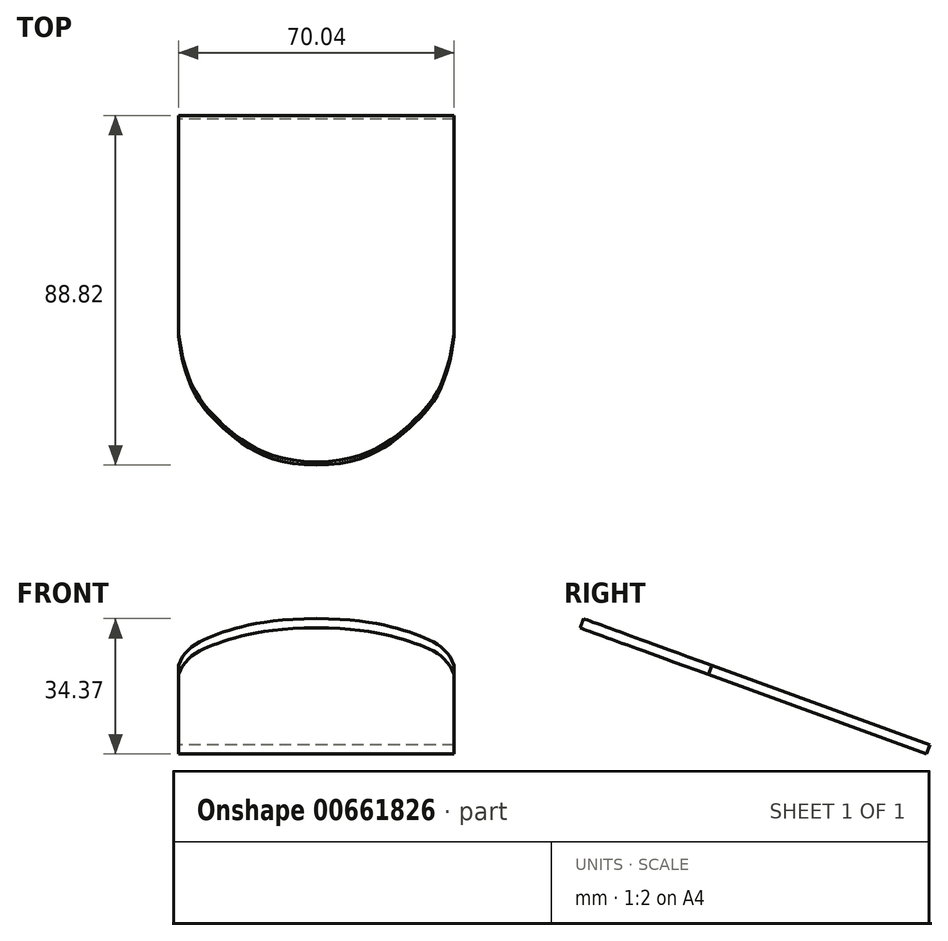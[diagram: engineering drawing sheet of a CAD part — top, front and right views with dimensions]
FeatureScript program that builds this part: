
annotation { "Feature Type Name" : "Feature", "Feature Type Description" : "" }
export const myFeature = defineFeature(function(context is Context, id is Id, definition is map)
    precondition{}
    {
        {
            var Q0;
            Q0=qCreatedBy(makeId("Top.planeOp"),FACE);
            cPlane(context, id + "F0", {"entities" : qUnion([Q0]), "cplaneType" : CPlaneType.OFFSET, "offset" : 20 * mm, "oppositeDirection" : true, "width" : 150 * mm, "height" : 150 * mm});
        }
        {
            var Q0;
            Q0=qCreatedBy(id+"F0.planeOp",FACE);
            cPlane(context, id + "F1", {"entities" : qUnion([Q0]), "cplaneType" : CPlaneType.OFFSET, "offset" : 50 * mm, "oppositeDirection" : true, "width" : 150 * mm, "height" : 150 * mm});
        }
        {
            var Q0;
            Q0=qCreatedBy(makeId("Right.planeOp"),FACE);
            var sketch = newSketch(context, id + "F2", { "sketchPlane" : qUnion([Q0])});
            skLineSegment(sketch, "E0", {"start": v(0, 15.18) * mm, "end": v(0, -94.42) * mm, "construction": true});
            skSolve(sketch);
        }
        {
            var Q0;
            Q0=qCreatedBy(id+"F1.planeOp",FACE);
            var sketch = newSketch(context, id + "F3", { "sketchPlane" : qUnion([Q0])});
            skLineSegment(sketch, "E1", {"start": v(-73.4, 0) * mm, "end": v(89.46, 0) * mm, "construction": true});
            skSolve(sketch);
        }
        {
            var Q0;
            Q0=sQuery(id+"F3.wireOp",EDGE,"E1");
            cPlane(context, id + "F4", {"entities" : qUnion([Q0]), "cplaneType" : CPlaneType.LINE_ANGLE, "offset" : 25 * mm, "angle" : 70 * degree, "width" : 150 * mm, "height" : 150 * mm});
        }
        {
            var Q0;
            Q0=qCreatedBy(id+"F4.planeOp",FACE);
            var sketch = newSketch(context, id + "F5", { "sketchPlane" : qUnion([Q0])});
            skFitSpline(sketch, "E2", {"points": [v(0, -10.76) * mm, v(-24.39, 0) * mm, v(-35.02, 23.96) * mm], "startDerivative": vector(-74.23, -0.1) * mm, "endDerivative": vector(-10.58, 83.32) * mm});
            skFitSpline(sketch, "E3.MirrorCS", {"points": [v(0, -10.76) * mm, v(24.39, 0) * mm, v(35.02, 23.96) * mm], "startDerivative": vector(74.23, -0.1) * mm, "endDerivative": vector(10.58, 83.32) * mm});
            skLineSegment(sketch, "E4", {"start": v(-35.02, 23.96) * mm, "end": v(-35.02, 82.85) * mm});
            skLineSegment(sketch, "E5", {"start": v(35.02, 23.96) * mm, "end": v(35.02, 82.85) * mm});
            skLineSegment(sketch, "E6", {"start": v(35.02, 82.85) * mm, "end": v(-35.02, 82.85) * mm});
            skSolve(sketch);
        }
        {
            var Q0;
            Q0 = qSketchRegion(id + "F5", true);
            extrude(context, id + "F6", {"entities" : qUnion([Q0]), "depth" : 2.5 * mm, "offsetDistance" : 25 * mm});
        }
    });
